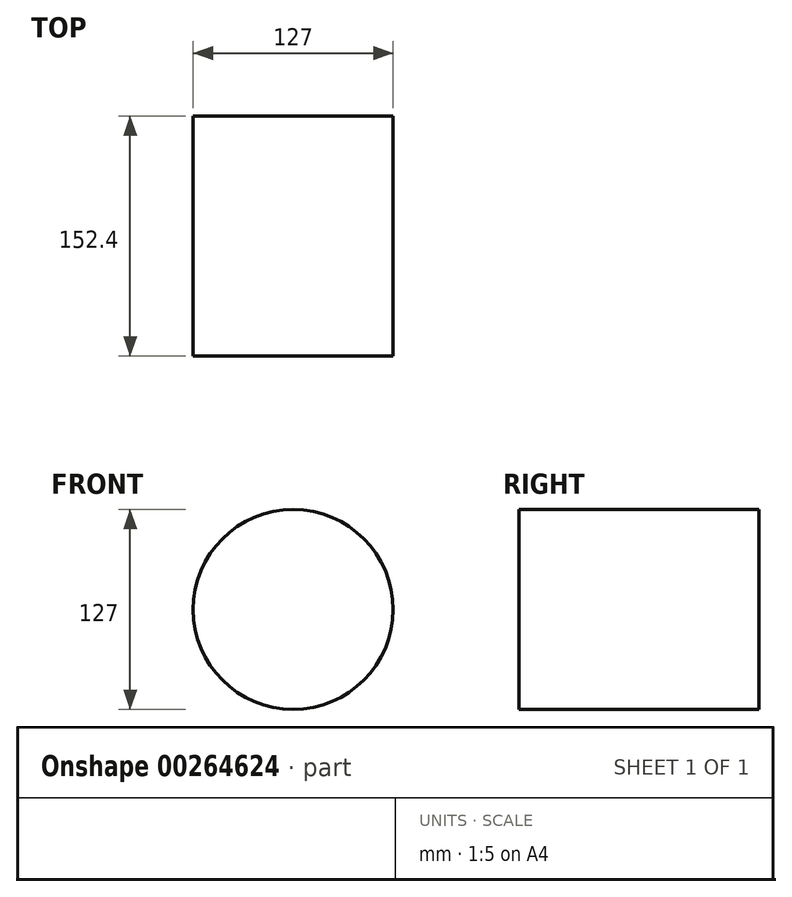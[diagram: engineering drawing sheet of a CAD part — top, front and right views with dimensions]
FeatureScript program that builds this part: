
annotation { "Feature Type Name" : "Feature", "Feature Type Description" : "" }
export const myFeature = defineFeature(function(context is Context, id is Id, definition is map)
    precondition{}
    {
        {
            var Q0;
            Q0=qCreatedBy(makeId("Front.planeOp"),FACE);
            var sketch = newSketch(context, id + "F0", { "sketchPlane" : qUnion([Q0])});
            skCircle(sketch, "E0", {"center": v(0, 0) * mm, "radius": 63.5 * mm});
            skSolve(sketch);
        }
        {
            var Q0;
            Q0 = qSketchRegion(id + "F0", true);
            extrude(context, id + "F1", {"entities" : qUnion([Q0]), "depth" : 152.4 * mm});
        }
    });
